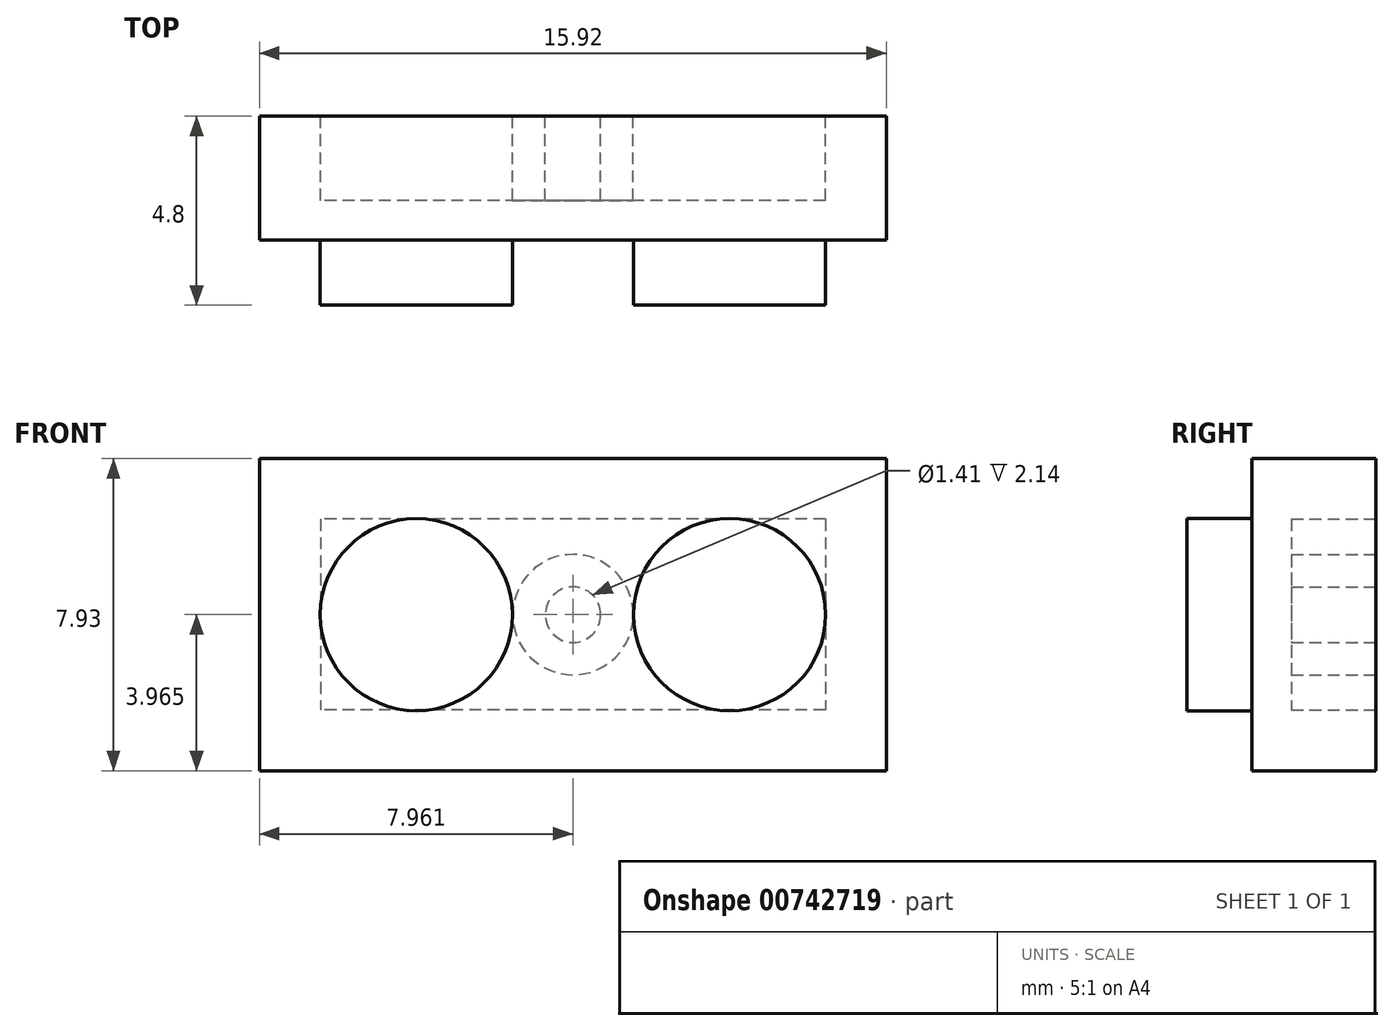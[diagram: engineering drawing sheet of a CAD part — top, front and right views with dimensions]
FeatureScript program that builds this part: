
annotation { "Feature Type Name" : "Feature", "Feature Type Description" : "" }
export const myFeature = defineFeature(function(context is Context, id is Id, definition is map)
    precondition{}
    {
        {
            var Q0;
            Q0=qCreatedBy(makeId("Front.planeOp"),FACE);
            var sketch = newSketch(context, id + "F0", { "sketchPlane" : qUnion([Q0])});
            skLineSegment(sketch, "E0.bottom", {"start": v(-13.79, 8.32) * mm, "end": v(2.13, 8.32) * mm});
            skLineSegment(sketch, "E0.top", {"start": v(-13.79, 0.4) * mm, "end": v(2.13, 0.4) * mm});
            skLineSegment(sketch, "E0.left", {"start": v(-13.79, 8.32) * mm, "end": v(-13.79, 0.4) * mm});
            skLineSegment(sketch, "E0.right", {"start": v(2.13, 8.32) * mm, "end": v(2.13, 0.4) * mm});
            skCircle(sketch, "E1", {"center": v(-9.8, 4.36) * mm, "radius": 2.44 * mm});
            skPoint(sketch, "E1.centerSnap0", {"position": v(-13.79, 4.36) * mm});
            skPoint(sketch, "E1.centerSnap1", {"position": v(-9.8, 8.32) * mm});
            skCircle(sketch, "E2", {"center": v(-1.85, 4.36) * mm, "radius": 2.44 * mm});
            skPoint(sketch, "E2.centerSnap0", {"position": v(2.13, 4.36) * mm});
            skPoint(sketch, "E2.centerSnap1", {"position": v(-1.85, 8.32) * mm});
            skPoint(sketch, "E3.end.orphan", {"position": v(-5.83, 0.4) * mm});
            skPoint(sketch, "E3.start.orphan", {"position": v(-5.83, 8.32) * mm});
            skPoint(sketch, "E4.start.orphan", {"position": v(-13.79, -1.15) * mm});
            skLineSegment(sketch, "E5", {"start": v(-7.93, 0.4) * mm, "end": v(-3.75, 0.4) * mm});
            skLineSegment(sketch, "E6", {"start": v(-7.93, 0.4) * mm, "end": v(-10.39, 0.4) * mm});
            skLineSegment(sketch, "E7", {"start": v(-3.75, 0.4) * mm, "end": v(-1.29, 0.4) * mm});
            skLineSegment(sketch, "E8.bottom", {"start": v(-10.39, 0.4) * mm, "end": v(-7.93, 0.4) * mm});
            skSolve(sketch);
        }
        {
            var Q0;
            Q0 = qSketchRegion(id + "F0", true);
            var Q1;
            Q1=makeQuery(id+"F0.imprint","IMPRINT",FACE,{"disambiguationData":[TD([[makeQuery(id+"F0.imprint","IMPRINT",EDGE,{"derivedFrom":sQuery(id+"F0.wireOp",EDGE,"E0.bottom")}),-1.0]])]});
            extrude(context, id + "F1", {"entities" : qUnion([Q0, Q1]), "depth" : 3.15 * mm, "offsetDistance" : 25 * mm});
        }
        {
            var Q0;
            Q0=makeQuery(id+"F0.imprint","IMPRINT",FACE,{"disambiguationData":[TD([[makeQuery(id+"F0.imprint","IMPRINT",EDGE,{"derivedFrom":sQuery(id+"F0.wireOp",EDGE,"E1")}),1.0]])]});
            var Q1;
            Q1=makeQuery(id+"F0.imprint","IMPRINT",FACE,{"disambiguationData":[TD([[makeQuery(id+"F0.imprint","IMPRINT",EDGE,{"derivedFrom":sQuery(id+"F0.wireOp",EDGE,"E2")}),1.0]])]});
            extrude(context, id + "F2", {"entities" : qUnion([Q0, Q1]), "operationType" : NewBodyOperationType.ADD, "depth" : 4.8 * mm, "offsetDistance" : 25 * mm});
        }
        {
            var Q0;
            {var subQ0=sQuery(id+"F0.wireOp",EDGE,"E2");var subQ1=sQuery(id+"F0.wireOp",EDGE,"E1");Q0=makeQuery(id+"F2.boolean.opBoolean","MERGE",FACE,{"derivedFrom":[makeQuery(id+"F1.opExtrude","CAP_FACE",FACE,{"disambiguationData":[OSD([sQuery(id+"F0.wireOp",EDGE,"E0.bottom"),sQuery(id+"F0.wireOp",EDGE,"E0.top"),sQuery(id+"F0.wireOp",EDGE,"E0.left"),sQuery(id+"F0.wireOp",EDGE,"E0.right"),subQ1,subQ0,sQuery(id+"F0.wireOp",EDGE,"E5"),sQuery(id+"F0.wireOp",EDGE,"E8.bottom"),sQuery(id+"F0.wireOp",EDGE,"E7")])],"isStart":true}),makeQuery(id+"F2.opExtrude","CAP_FACE",FACE,{"disambiguationData":[OSD([subQ1])],"isStart":true}),makeQuery(id+"F2.opExtrude","CAP_FACE",FACE,{"disambiguationData":[OSD([subQ0])],"isStart":true})]});}
            var sketch = newSketch(context, id + "F3", { "sketchPlane" : qUnion([Q0])});
            skLineSegment(sketch, "E9.bottom", {"start": v(-0.58, 6.78) * mm, "end": v(12.24, 6.78) * mm});
            skLineSegment(sketch, "E9.top", {"start": v(-0.58, 1.93) * mm, "end": v(12.24, 1.93) * mm});
            skLineSegment(sketch, "E9.left", {"start": v(-0.58, 6.78) * mm, "end": v(-0.58, 1.93) * mm});
            skLineSegment(sketch, "E9.right", {"start": v(12.24, 6.78) * mm, "end": v(12.24, 1.93) * mm});
            skCircle(sketch, "E10", {"center": v(5.83, 4.36) * mm, "radius": 1.53 * mm});
            skCircle(sketch, "E11", {"center": v(5.83, 4.36) * mm, "radius": 0.7 * mm});
            skPoint(sketch, "E12.start.orphan", {"position": v(-0.8, 5.39) * mm});
            skPoint(sketch, "E13.start.orphan", {"position": v(4.5, 7.29) * mm});
            skPoint(sketch, "E14.trimOffspring.end.orphan", {"position": v(7.15, 1.42) * mm});
            skPoint(sketch, "E15.trimOffspring.end.orphan", {"position": v(15.11, 5.39) * mm});
            skLineSegment(sketch, "E16.bottom", {"start": v(-2.13, 8.32) * mm, "end": v(13.79, 8.32) * mm});
            skLineSegment(sketch, "E16.top", {"start": v(-2.13, 0.4) * mm, "end": v(13.79, 0.4) * mm});
            skLineSegment(sketch, "E16.left", {"start": v(-2.13, 8.32) * mm, "end": v(-2.13, 0.4) * mm});
            skLineSegment(sketch, "E16.right", {"start": v(13.79, 8.32) * mm, "end": v(13.79, 0.4) * mm});
            skPoint(sketch, "E17.start.orphan", {"position": v(5.83, 8.32) * mm});
            skPoint(sketch, "E18.trimOffspring.end.orphan", {"position": v(13.79, 4.36) * mm});
            skPoint(sketch, "E19.start.orphan", {"position": v(-2.13, 4.36) * mm});
            skPoint(sketch, "E20.trimOffspring.end.orphan", {"position": v(5.83, 0.4) * mm});
            skSolve(sketch);
        }
        {
            var Q0;
            Q0=makeQuery(id+"F3.imprint","IMPRINT",FACE,{"disambiguationData":[TD([[makeQuery(id+"F3.imprint","IMPRINT",EDGE,{"derivedFrom":sQuery(id+"F3.wireOp",EDGE,"E9.left")}),1.0]])]});
            var Q1;
            Q1=makeQuery(id+"F3.imprint","IMPRINT",FACE,{"disambiguationData":[TD([[makeQuery(id+"F3.imprint","IMPRINT",EDGE,{"derivedFrom":sQuery(id+"F3.wireOp",EDGE,"E11")}),1.0]])]});
            extrude(context, id + "F4", {"entities" : qUnion([Q0, Q1]), "operationType" : NewBodyOperationType.REMOVE, "oppositeDirection" : true, "depth" : 2.14 * mm, "offsetDistance" : 25 * mm});
        }
    });
